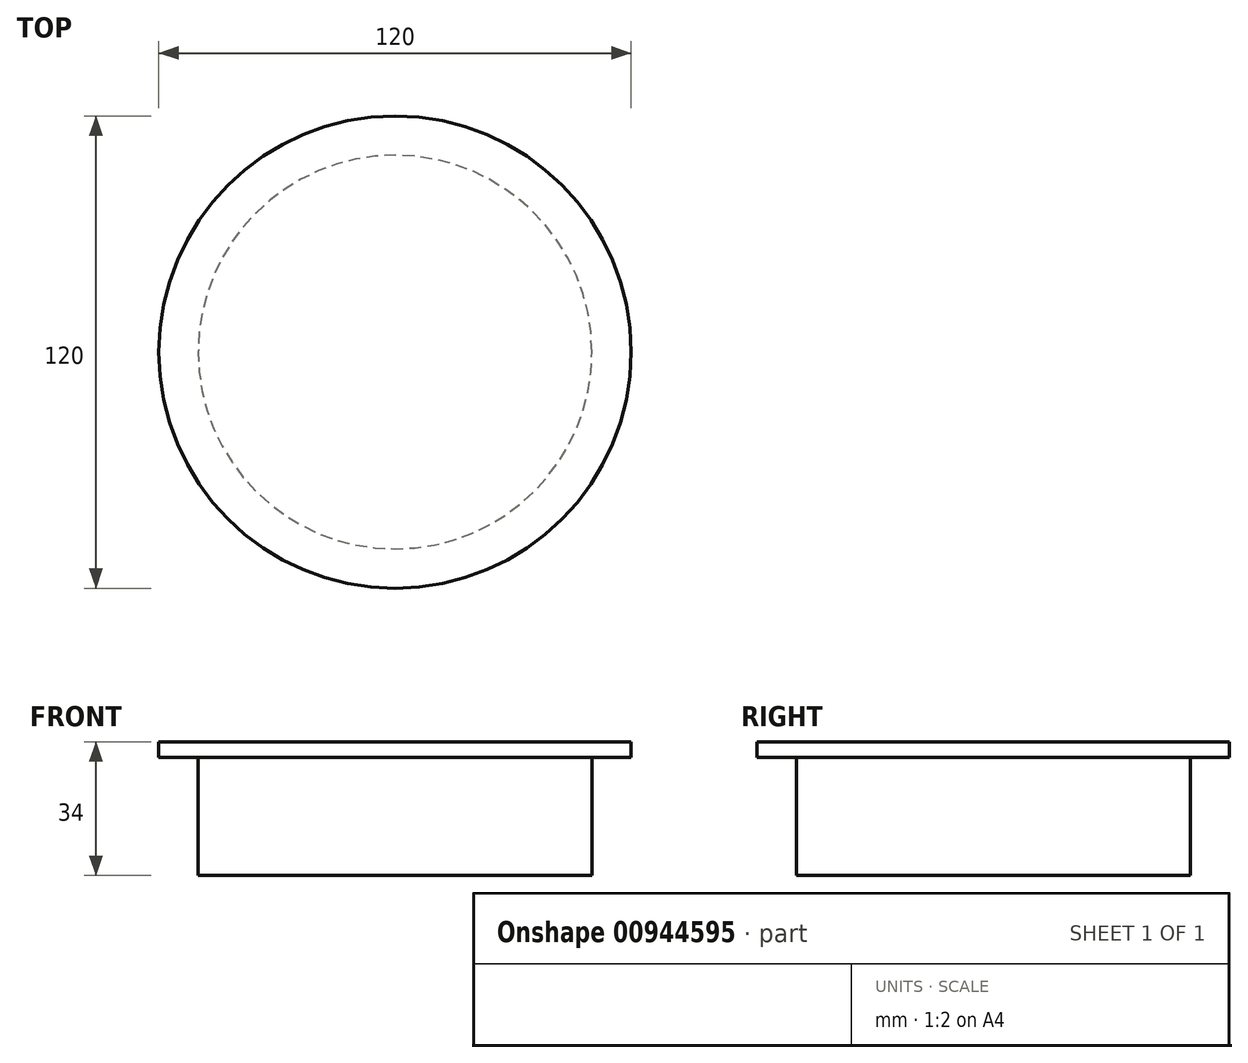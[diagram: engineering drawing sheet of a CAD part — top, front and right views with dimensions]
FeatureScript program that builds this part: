
annotation { "Feature Type Name" : "Feature", "Feature Type Description" : "" }
export const myFeature = defineFeature(function(context is Context, id is Id, definition is map)
    precondition{}
    {
        {
            var Q0;
            Q0=qCreatedBy(makeId("Right.planeOp"),FACE);
            var sketch = newSketch(context, id + "F0", { "sketchPlane" : qUnion([Q0])});
            skLineSegment(sketch, "E0", {"start": v(0, 0) * mm, "end": v(-50, 0) * mm});
            skLineSegment(sketch, "E1", {"start": v(-50, 0) * mm, "end": v(-50, 30) * mm});
            skLineSegment(sketch, "E2", {"start": v(-50, 30) * mm, "end": v(-60, 30) * mm});
            skLineSegment(sketch, "E3", {"start": v(-60, 30) * mm, "end": v(-60, 34) * mm});
            skLineSegment(sketch, "E4", {"start": v(-60, 34) * mm, "end": v(0, 34) * mm});
            skLineSegment(sketch, "E5", {"start": v(0, 34) * mm, "end": v(0, 0) * mm});
            skLineSegment(sketch, "E6", {"start": v(0, -5.78) * mm, "end": v(0, 0) * mm});
            skSolve(sketch);
        }
        {
            var Q0;
            Q0=qCreatedBy(makeId("Right.planeOp"),FACE);
            var sketch = newSketch(context, id + "F1", { "sketchPlane" : qUnion([Q0])});
            skLineSegment(sketch, "E7", {"start": v(0, 34.27) * mm, "end": v(0, 11.75) * mm});
            skLineSegment(sketch, "E8", {"start": v(0, 11.75) * mm, "end": v(-43.93, 11.75) * mm});
            skLineSegment(sketch, "E9", {"start": v(-43.93, 11.75) * mm, "end": v(-43.93, 33.83) * mm});
            skLineSegment(sketch, "E10", {"start": v(-43.93, 33.83) * mm, "end": v(0, 34.27) * mm});
            skSolve(sketch);
        }
        {
            var Q0;
            Q0=makeQuery(id+"F0.imprint","IMPRINT",FACE,{"disambiguationData":[TD([[makeQuery(id+"F0.imprint","IMPRINT",EDGE,{"derivedFrom":sQuery(id+"F0.wireOp",EDGE,"E0")}),-1.0]])]});
            var Q1;
            Q1=sQuery(id+"F1.wireOp",EDGE,"E7");
            revolve(context, id + "F2", {"surfaceOperationType" : NewSurfaceOperationType.NEW, "entities" : qUnion([Q0]), "axis" : qUnion([Q1]), "revolveType" : RevolveType.FULL});
        }
    });
